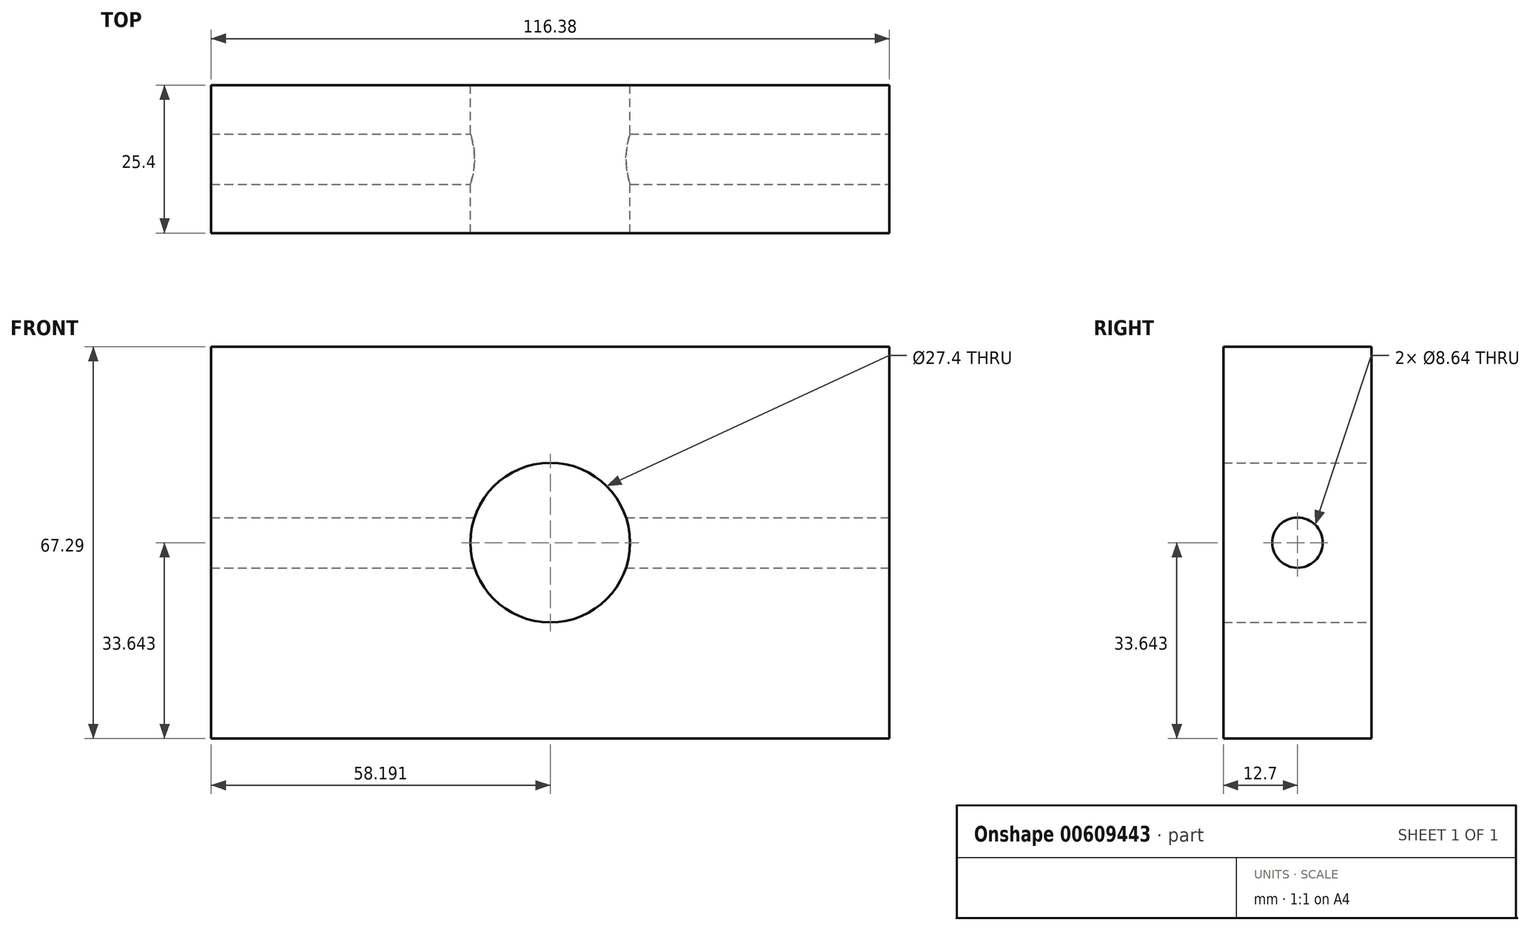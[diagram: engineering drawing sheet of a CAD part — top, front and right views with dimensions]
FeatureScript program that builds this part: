
annotation { "Feature Type Name" : "Feature", "Feature Type Description" : "" }
export const myFeature = defineFeature(function(context is Context, id is Id, definition is map)
    precondition{}
    {
        {
            var Q0;
            Q0=qCreatedBy(makeId("Front.planeOp"),FACE);
            var sketch = newSketch(context, id + "F0", { "sketchPlane" : qUnion([Q0])});
            skLineSegment(sketch, "E0.bottom", {"start": v(0, 0) * mm, "end": v(116.38, 0) * mm});
            skLineSegment(sketch, "E0.top", {"start": v(0, 67.29) * mm, "end": v(116.38, 67.29) * mm});
            skLineSegment(sketch, "E0.left", {"start": v(0, 0) * mm, "end": v(0, 67.29) * mm});
            skLineSegment(sketch, "E0.right", {"start": v(116.38, 0) * mm, "end": v(116.38, 67.29) * mm});
            skCircle(sketch, "E1", {"center": v(58.2, 33.64) * mm, "radius": 13.7 * mm});
            skPoint(sketch, "E1.centerSnap0", {"position": v(0, 33.64) * mm});
            skPoint(sketch, "E1.centerSnap1", {"position": v(58.2, 67.29) * mm});
            skSolve(sketch);
        }
        {
            var Q0;
            Q0 = qSketchRegion(id + "F0", true);
            extrude(context, id + "F1", {"entities" : qUnion([Q0]), "depth" : 25.4 * mm, "offsetDistance" : 25.4 * mm});
        }
        {
            var Q0;
            Q0=makeQuery(id+"F1.opExtrude","SWEPT_FACE",FACE,{"disambiguationData":[OSD([sQuery(id+"F0.wireOp",EDGE,"E0.right")])]});
            var sketch = newSketch(context, id + "F2", { "sketchPlane" : qUnion([Q0])});
            skCircle(sketch, "E2", {"center": v(-12.7, 33.64) * mm, "radius": 4.32 * mm});
            skPoint(sketch, "E2.centerSnap0", {"position": v(-25.4, 33.64) * mm});
            skPoint(sketch, "E2.centerSnap1", {"position": v(-12.7, 67.29) * mm});
            skSolve(sketch);
        }
        {
            var Q0;
            Q0 = qSketchRegion(id + "F2", true);
            extrude(context, id + "F3", {"entities" : qUnion([Q0]), "operationType" : NewBodyOperationType.REMOVE, "oppositeDirection" : true, "depth" : 167.13 * mm, "offsetDistance" : 25.4 * mm});
        }
    });
